# Revit family: Sanitary_Wash-Basins_hansgrohe_22424CHN-MellowTide-Wash-bowl-675-395
name_source: partatom
category: Plumbing Fixtures
revit_build: Autodesk Revit 2018 (Build: 20190510_1515(x64)
units: mm (PartAtom-declared; Revit-internal decimal feet)

## family parameters
Cut with Voids When Loaded = No
Host = Face
OmniClass Number = 23.31.13.00
OmniClass Title = Sinks
Part Type = Normal
Room Calculation Point = No
Round Connector Dimension = Use Diameter
Shared = No

## types (1)
- 007 White
    Always visible = Yes
    BIMobject category = Wash Basins
    Default Elevation = 1219 mm
    Description = MellowTide Wash bowl 675/395
    Design country = Germany
    EAN code = 4059625384831
    Edition number = 1
    IFC Classification = Sanitary Terminal
    Installation instructions = https://www.hansgrohe.com
    Manufacturer = Hansgrohe
    Manufacturer country = Germany
    Manufacturer name = hansgrohe
    Material = Hansgrohe - Ceramic - 007 White
    Model = 22424CHN
    Product Guid = 792626bc-dcda-4253-b915-d1c80de38675
    Product SKU = 22424CHN
    Product data url = https://bimobject.com
    Product family = MellowTide
    Product group = Washbasins
    Product name = 22424CHN MellowTide Wash bowl 675/395
    Product url = https://www.hansgrohe.com
    QR code = https://bimobject.com
    URL = https://www.hansgrohe.com
    Water Outlet = 45  [stored 0.147638 ft]
    Water Outlet Description = Water Outlet 45mm
    Weight Net (Kg) = 13

note: [stored X ft] marks values corroborated as IEEE doubles in the binary element streams (Revit-internal decimal feet)

## geometry (parser evidence)
native form markers: Sweep x3
no freeform markers — native parametric forms only
